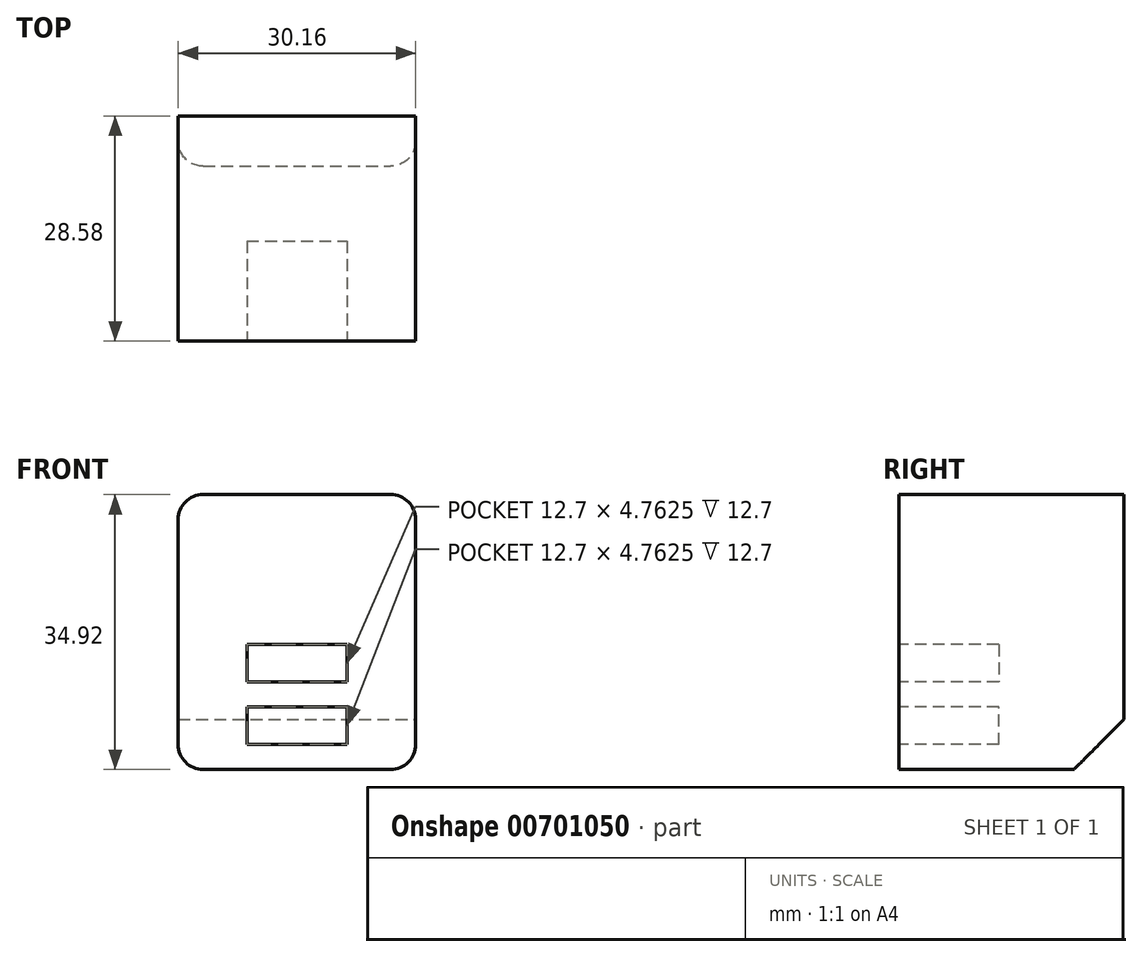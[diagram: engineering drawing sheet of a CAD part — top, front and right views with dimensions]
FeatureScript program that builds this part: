
annotation { "Feature Type Name" : "Feature", "Feature Type Description" : "" }
export const myFeature = defineFeature(function(context is Context, id is Id, definition is map)
    precondition{}
    {
        {
            var Q0;
            Q0=qCreatedBy(makeId("Front.planeOp"),FACE);
            var sketch = newSketch(context, id + "F0", { "sketchPlane" : qUnion([Q0])});
            skLineSegment(sketch, "E0.bottom", {"start": v(11.9, 17.46) * mm, "end": v(-11.9, 17.46) * mm});
            skLineSegment(sketch, "E0.top", {"start": v(11.9, -17.46) * mm, "end": v(-11.9, -17.46) * mm});
            skLineSegment(sketch, "E0.left", {"start": v(15.08, 14.29) * mm, "end": v(15.08, -14.29) * mm});
            skLineSegment(sketch, "E0.right", {"start": v(-15.08, 14.29) * mm, "end": v(-15.08, -14.29) * mm});
            skPoint(sketch, "E0.middle", {"position": v(0, 0) * mm});
            skPoint(sketch, "E1.visualSharp", {"position": v(-15.08, 17.46) * mm});
            skArc(sketch, "E1.filletArc", {"start": v(-11.9, 17.46) * mm, "mid": v(-14.15, 16.53) * mm, "end": v(-15.08, 14.29) * mm});
            skPoint(sketch, "E2.visualSharp", {"position": v(15.08, 17.46) * mm});
            skArc(sketch, "E2.filletArc", {"start": v(15.08, 14.29) * mm, "mid": v(14.15, 16.53) * mm, "end": v(11.9, 17.46) * mm});
            skPoint(sketch, "E3.visualSharp", {"position": v(15.08, -17.46) * mm});
            skArc(sketch, "E3.filletArc", {"start": v(11.9, -17.46) * mm, "mid": v(14.15, -16.53) * mm, "end": v(15.08, -14.29) * mm});
            skPoint(sketch, "E4.visualSharp", {"position": v(-15.08, -17.46) * mm});
            skArc(sketch, "E4.filletArc", {"start": v(-15.08, -14.29) * mm, "mid": v(-14.15, -16.53) * mm, "end": v(-11.9, -17.46) * mm});
            skSolve(sketch);
        }
        {
            var Q0;
            Q0 = qSketchRegion(id + "F0", true);
            extrude(context, id + "F1", {"entities" : qUnion([Q0]), "oppositeDirection" : true, "depth" : 28.57 * mm, "offsetDistance" : 25.4 * mm});
        }
        {
            var Q0;
            Q0=makeQuery(id+"F1.opExtrude","SWEPT_FACE",FACE,{"disambiguationData":[OSD([sQuery(id+"F0.wireOp",EDGE,"E0.left")])]});
            var sketch = newSketch(context, id + "F2", { "sketchPlane" : qUnion([Q0])});
            skLineSegment(sketch, "E5", {"start": v(28.58, -11.11) * mm, "end": v(28.58, -17.46) * mm});
            skLineSegment(sketch, "E6", {"start": v(28.58, -17.46) * mm, "end": v(22.23, -17.46) * mm});
            skLineSegment(sketch, "E7", {"start": v(22.23, -17.46) * mm, "end": v(28.58, -11.11) * mm});
            skSolve(sketch);
        }
        {
            var Q0;
            Q0 = qSketchRegion(id + "F2", true);
            extrude(context, id + "F3", {"entities" : qUnion([Q0]), "operationType" : NewBodyOperationType.REMOVE, "endBound" : BoundingType.THROUGH_ALL, "oppositeDirection" : true, "depth" : 25.4 * mm, "offsetDistance" : 25.4 * mm});
        }
        {
            var Q0;
            Q0=makeQuery(id+"F1.opExtrude","CAP_FACE",FACE,{"disambiguationData":[OSD([sQuery(id+"F0.wireOp",EDGE,"E0.bottom"),sQuery(id+"F0.wireOp",EDGE,"E0.top"),sQuery(id+"F0.wireOp",EDGE,"E0.left"),sQuery(id+"F0.wireOp",EDGE,"E0.right"),sQuery(id+"F0.wireOp",EDGE,"E1.filletArc"),sQuery(id+"F0.wireOp",EDGE,"E2.filletArc"),sQuery(id+"F0.wireOp",EDGE,"E3.filletArc"),sQuery(id+"F0.wireOp",EDGE,"E4.filletArc")])],"isStart":false});
            var sketch = newSketch(context, id + "F4", { "sketchPlane" : qUnion([Q0])});
            skLineSegment(sketch, "E8.bottom", {"start": v(-8.73, -1.59) * mm, "end": v(-5.56, -1.59) * mm});
            skLineSegment(sketch, "E8.top", {"start": v(-8.73, -17.46) * mm, "end": v(-5.56, -17.46) * mm});
            skLineSegment(sketch, "E8.left", {"start": v(-8.73, -1.59) * mm, "end": v(-8.73, -17.46) * mm});
            skLineSegment(sketch, "E8.right", {"start": v(-5.56, -1.59) * mm, "end": v(-5.56, -17.46) * mm});
            skLineSegment(sketch, "E9.MirrorCS", {"start": v(5.56, -1.59) * mm, "end": v(5.56, -17.46) * mm});
            skLineSegment(sketch, "E10.MirrorCS", {"start": v(8.73, -1.59) * mm, "end": v(5.56, -1.59) * mm});
            skLineSegment(sketch, "E11.MirrorCS", {"start": v(8.73, -1.59) * mm, "end": v(8.73, -17.46) * mm});
            skLineSegment(sketch, "E12.MirrorCS", {"start": v(8.73, -17.46) * mm, "end": v(5.56, -17.46) * mm});
            skSolve(sketch);
        }
        {
            var Q0;
            Q0=makeQuery(id+"F1.opExtrude","CAP_FACE",FACE,{"disambiguationData":[OSD([sQuery(id+"F0.wireOp",EDGE,"E0.bottom"),sQuery(id+"F0.wireOp",EDGE,"E0.top"),sQuery(id+"F0.wireOp",EDGE,"E0.left"),sQuery(id+"F0.wireOp",EDGE,"E0.right"),sQuery(id+"F0.wireOp",EDGE,"E1.filletArc"),sQuery(id+"F0.wireOp",EDGE,"E2.filletArc"),sQuery(id+"F0.wireOp",EDGE,"E3.filletArc"),sQuery(id+"F0.wireOp",EDGE,"E4.filletArc")])],"isStart":false});
            var sketch = newSketch(context, id + "F5", { "sketchPlane" : qUnion([Q0])});
            skLineSegment(sketch, "E13.bottom", {"start": v(-7.94, -1.59) * mm, "end": v(-6.35, -1.59) * mm});
            skLineSegment(sketch, "E13.top", {"start": v(-7.94, 4.76) * mm, "end": v(-6.35, 4.76) * mm});
            skLineSegment(sketch, "E13.left", {"start": v(-7.94, -1.59) * mm, "end": v(-7.94, 4.76) * mm});
            skLineSegment(sketch, "E13.right", {"start": v(-6.35, -1.59) * mm, "end": v(-6.35, 4.76) * mm});
            skLineSegment(sketch, "E14.MirrorCS", {"start": v(6.35, -1.59) * mm, "end": v(6.35, 4.76) * mm});
            skLineSegment(sketch, "E15.MirrorCS", {"start": v(7.94, 4.76) * mm, "end": v(6.35, 4.76) * mm});
            skLineSegment(sketch, "E16.MirrorCS", {"start": v(7.94, -1.59) * mm, "end": v(7.94, 4.76) * mm});
            skLineSegment(sketch, "E17.MirrorCS", {"start": v(7.94, -1.59) * mm, "end": v(6.35, -1.59) * mm});
            skLineSegment(sketch, "E18", {"start": v(0, 17.46) * mm, "end": v(0, -11.11) * mm, "construction": true});
            skSolve(sketch);
        }
        {
            var Q0;
            Q0=makeQuery(id+"F1.opExtrude","CAP_FACE",FACE,{"disambiguationData":[OSD([sQuery(id+"F0.wireOp",EDGE,"E0.bottom"),sQuery(id+"F0.wireOp",EDGE,"E0.top"),sQuery(id+"F0.wireOp",EDGE,"E0.left"),sQuery(id+"F0.wireOp",EDGE,"E0.right"),sQuery(id+"F0.wireOp",EDGE,"E1.filletArc"),sQuery(id+"F0.wireOp",EDGE,"E2.filletArc"),sQuery(id+"F0.wireOp",EDGE,"E3.filletArc"),sQuery(id+"F0.wireOp",EDGE,"E4.filletArc")])],"isStart":true});
            var sketch = newSketch(context, id + "F6", { "sketchPlane" : qUnion([Q0])});
            skLineSegment(sketch, "E19.bottom", {"start": v(-6.35, -14.29) * mm, "end": v(6.35, -14.29) * mm});
            skLineSegment(sketch, "E19.top", {"start": v(-6.35, -9.53) * mm, "end": v(6.35, -9.53) * mm});
            skLineSegment(sketch, "E19.left", {"start": v(-6.35, -14.29) * mm, "end": v(-6.35, -9.53) * mm});
            skLineSegment(sketch, "E19.right", {"start": v(6.35, -14.29) * mm, "end": v(6.35, -9.53) * mm});
            skPoint(sketch, "E19.middle", {"position": v(0, -11.9) * mm});
            skLineSegment(sketch, "E20.bottom", {"start": v(-6.35, -1.59) * mm, "end": v(6.35, -1.59) * mm});
            skLineSegment(sketch, "E20.top", {"start": v(-6.35, -6.35) * mm, "end": v(6.35, -6.35) * mm});
            skLineSegment(sketch, "E20.left", {"start": v(-6.35, -1.59) * mm, "end": v(-6.35, -6.35) * mm});
            skLineSegment(sketch, "E20.right", {"start": v(6.35, -1.59) * mm, "end": v(6.35, -6.35) * mm});
            skPoint(sketch, "E20.middle", {"position": v(0, -3.97) * mm});
            skSolve(sketch);
        }
        {
            var Q0;
            Q0=makeQuery(id+"F6.imprint","IMPRINT",FACE,{"disambiguationData":[TD([[makeQuery(id+"F6.imprint","IMPRINT",EDGE,{"derivedFrom":sQuery(id+"F6.wireOp",EDGE,"E19.bottom")}),1.0]])]});
            var Q1;
            Q1=makeQuery(id+"F6.imprint","IMPRINT",FACE,{"disambiguationData":[TD([[makeQuery(id+"F6.imprint","IMPRINT",EDGE,{"derivedFrom":sQuery(id+"F6.wireOp",EDGE,"E20.bottom")}),-1.0]])]});
            extrude(context, id + "F7", {"entities" : qUnion([Q0, Q1]), "operationType" : NewBodyOperationType.REMOVE, "oppositeDirection" : true, "depth" : 12.7 * mm, "offsetDistance" : 25.4 * mm});
        }
    });
